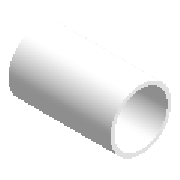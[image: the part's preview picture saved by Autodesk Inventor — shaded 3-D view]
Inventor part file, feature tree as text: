
AUTODESK INVENTOR PART (.ipt)
format: ipt  version: 2023 (Build 270158000, 158)  size: 157,696 bytes
history: native  units: mm (DEFAULTED — no unit token found)
features: other x6, revolve x1, sketch x1
ambient origin geometry x8: Origin, YZ Plane, XZ Plane, XY Plane, X Axis, Y Axis, Z Axis, Center Point
bodies: Solid1 (feature_tree)
feature tree (8):
  revolve  "Revolution1"  [1 undecoded]
  other  "Work Point1"
  other  "Work Point2"
  other  "Work Axis1"
  other  "Work Point3"
  other  "Work Axis2"
  other  "Work Point4"
  sketch  "Sketch1"  dims[d1=40.0mm d0=40.0mm d2=3.0mm d3=3.0mm d4=26.0mm d5=3.0mm d7=90.0deg]
note: 1 required parameter value undecoded (feature->parameter linkage not recoverable at this tier; creation-order binding heuristic only, values carry confidence <= 0.55)
